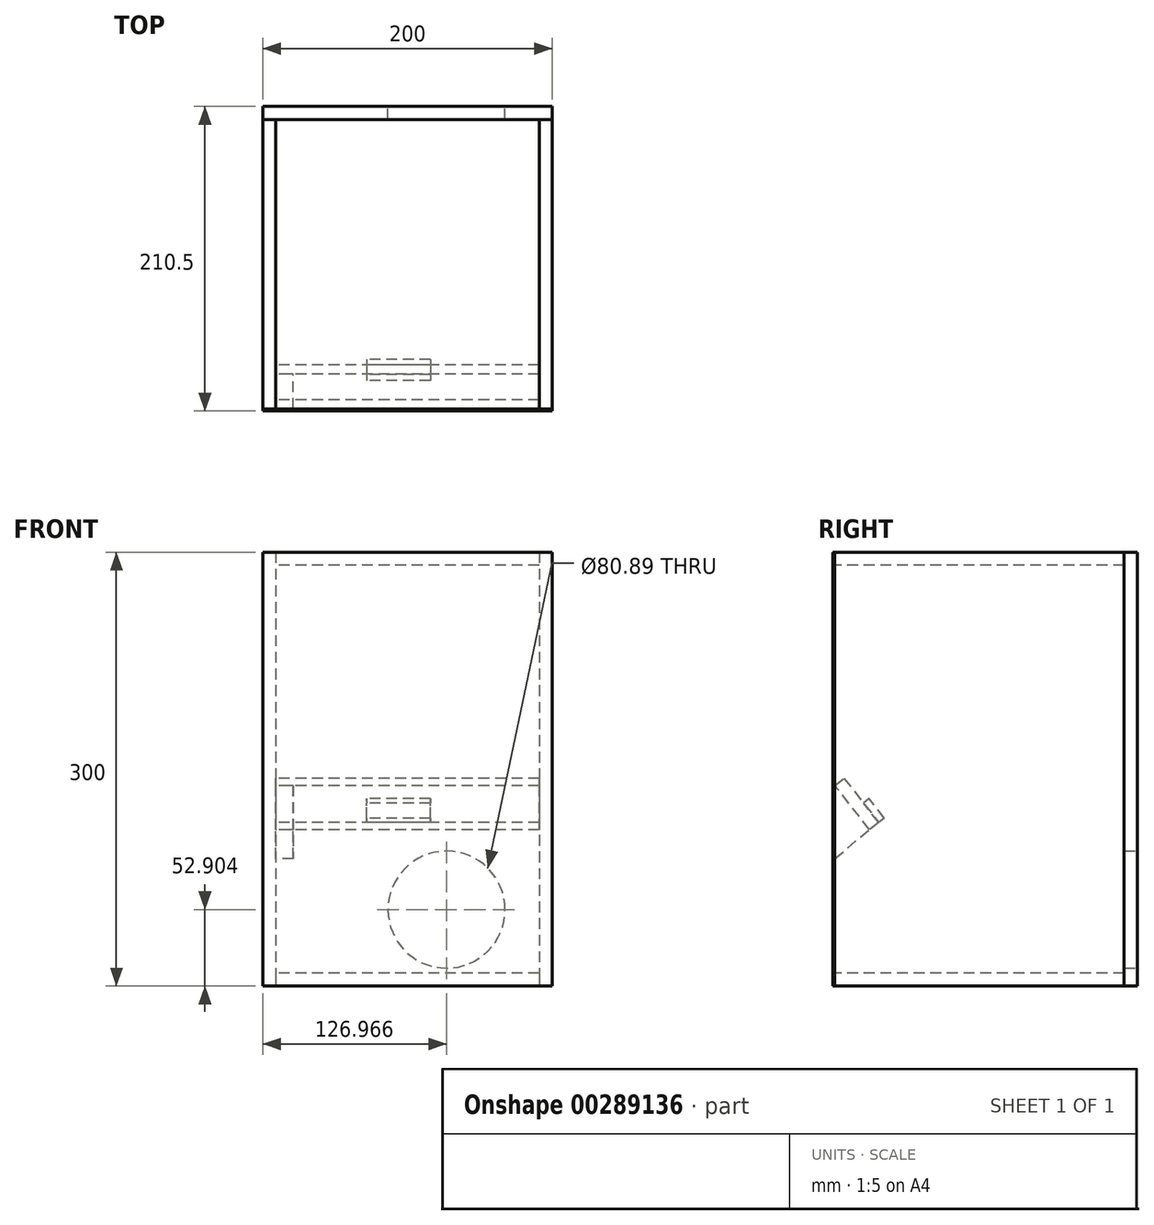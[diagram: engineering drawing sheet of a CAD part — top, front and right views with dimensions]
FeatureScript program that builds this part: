
annotation { "Feature Type Name" : "Feature", "Feature Type Description" : "" }
export const myFeature = defineFeature(function(context is Context, id is Id, definition is map)
    precondition{}
    {
        {
            var Q0;
            Q0=qCreatedBy(makeId("Front.planeOp"),FACE);
            var sketch = newSketch(context, id + "F0", { "sketchPlane" : qUnion([Q0])});
            skLineSegment(sketch, "E0.bottom", {"start": v(0, 0) * mm, "end": v(200, 0) * mm});
            skLineSegment(sketch, "E0.top", {"start": v(0, 300) * mm, "end": v(200, 300) * mm});
            skLineSegment(sketch, "E0.left", {"start": v(0, 0) * mm, "end": v(0, 300) * mm});
            skLineSegment(sketch, "E0.right", {"start": v(200, 0) * mm, "end": v(200, 300) * mm});
            skSolve(sketch);
        }
        {
            var Q0;
            Q0=qSketchRegion(id+"F0",true);
            extrude(context, id + "F1", {"entities" : qUnion([Q0]), "depth" : 1.5 * mm});
        }
        {
            var Q0;
            Q0=makeQuery(id+"F1.opExtrude","CAP_FACE",FACE,{"disambiguationData":[OSD([sQuery(id+"F0.wireOp",EDGE,"E0.bottom"),sQuery(id+"F0.wireOp",EDGE,"E0.top"),sQuery(id+"F0.wireOp",EDGE,"E0.left"),sQuery(id+"F0.wireOp",EDGE,"E0.right")])],"isStart":true});
            var sketch = newSketch(context, id + "F2", { "sketchPlane" : qUnion([Q0])});
            skLineSegment(sketch, "E1.bottom", {"start": v(0, 300) * mm, "end": v(-9, 300) * mm});
            skLineSegment(sketch, "E1.top", {"start": v(0, 0) * mm, "end": v(-9, 0) * mm});
            skLineSegment(sketch, "E1.left", {"start": v(0, 300) * mm, "end": v(0, 0) * mm});
            skLineSegment(sketch, "E1.right", {"start": v(-9, 300) * mm, "end": v(-9, 0) * mm});
            skSolve(sketch);
        }
        {
            var Q0;
            Q0=qSketchRegion(id+"F2",true);
            extrude(context, id + "F3", {"entities" : qUnion([Q0]), "depth" : 200 * mm});
        }
        {
            var Q0;
            Q0=makeQuery(id+"F3.opExtrude","SWEPT_FACE",FACE,{"disambiguationData":[OSD([sQuery(id+"F2.wireOp",EDGE,"E1.right")])]});
            var sketch = newSketch(context, id + "F4", { "sketchPlane" : qUnion([Q0])});
            skLineSegment(sketch, "E2", {"start": v(0, 138.7) * mm, "end": v(0, 88.15) * mm});
            skLineSegment(sketch, "E3", {"start": v(0, 88.15) * mm, "end": v(24, 108.1) * mm});
            skLineSegment(sketch, "E4", {"start": v(24, 108.1) * mm, "end": v(0, 138.7) * mm});
            skSolve(sketch);
        }
        {
            var Q0;
            Q0=qSketchRegion(id+"F4",true);
            extrude(context, id + "F5", {"entities" : qUnion([Q0]), "depth" : 12 * mm});
        }
        {
            var Q0;
            Q0=makeQuery(id+"F3.opExtrude","SWEPT_FACE",FACE,{"disambiguationData":[OSD([sQuery(id+"F2.wireOp",EDGE,"E1.right")])]});
            var sketch = newSketch(context, id + "F6", { "sketchPlane" : qUnion([Q0])});
            skLineSegment(sketch, "E5", {"start": v(24, 108.1) * mm, "end": v(0, 138.7) * mm});
            skLineSegment(sketch, "E6", {"start": v(0, 138.7) * mm, "end": v(6.36, 143.69) * mm});
            skLineSegment(sketch, "E7", {"start": v(6.36, 143.69) * mm, "end": v(30.36, 113.08) * mm});
            skLineSegment(sketch, "E8", {"start": v(30.36, 113.08) * mm, "end": v(24, 108.1) * mm});
            skSolve(sketch);
        }
        {
            var Q0;
            Q0=qSketchRegion(id+"F6",true);
            extrude(context, id + "F7", {"entities" : qUnion([Q0]), "depth" : 182 * mm});
        }
        {
            var Q0;
            Q0=makeQuery(id+"F7.opExtrude","SWEPT_FACE",FACE,{"disambiguationData":[OSD([sQuery(id+"F6.wireOp",EDGE,"E7")])]});
            var sketch = newSketch(context, id + "F8", { "sketchPlane" : qUnion([Q0])});
            skLineSegment(sketch, "E9.bottom", {"start": v(-115.8, 70.24) * mm, "end": v(-71.6, 70.24) * mm});
            skLineSegment(sketch, "E9.top", {"start": v(-115.8, 87.47) * mm, "end": v(-71.6, 87.47) * mm});
            skLineSegment(sketch, "E9.left", {"start": v(-115.8, 70.24) * mm, "end": v(-115.8, 87.47) * mm});
            skLineSegment(sketch, "E9.right", {"start": v(-71.6, 70.24) * mm, "end": v(-71.6, 87.47) * mm});
            skSolve(sketch);
        }
        {
            var Q0;
            Q0=qSketchRegion(id+"F8",true);
            extrude(context, id + "F9", {"entities" : qUnion([Q0]), "depth" : 5 * mm});
        }
        {
            var Q0;
            Q0=makeQuery(id+"F3.opExtrude","SWEPT_FACE",FACE,{"disambiguationData":[OSD([sQuery(id+"F2.wireOp",EDGE,"E1.right")])]});
            var sketch = newSketch(context, id + "F10", { "sketchPlane" : qUnion([Q0])});
            skLineSegment(sketch, "E10.bottom", {"start": v(200, 300) * mm, "end": v(0, 300) * mm});
            skLineSegment(sketch, "E10.top", {"start": v(200, 291) * mm, "end": v(0, 291) * mm});
            skLineSegment(sketch, "E10.left", {"start": v(200, 300) * mm, "end": v(200, 291) * mm});
            skLineSegment(sketch, "E10.right", {"start": v(0, 300) * mm, "end": v(0, 291) * mm});
            skSolve(sketch);
        }
        {
            var Q0;
            Q0=qSketchRegion(id+"F10",true);
            extrude(context, id + "F11", {"entities" : qUnion([Q0]), "depth" : 182 * mm});
        }
        {
            var Q0;
            Q0=makeQuery(id+"F3.opExtrude","SWEPT_FACE",FACE,{"disambiguationData":[OSD([sQuery(id+"F2.wireOp",EDGE,"E1.right")])]});
            var sketch = newSketch(context, id + "F12", { "sketchPlane" : qUnion([Q0])});
            skLineSegment(sketch, "E11.bottom", {"start": v(200, 0) * mm, "end": v(0, 0) * mm});
            skLineSegment(sketch, "E11.top", {"start": v(200, 9) * mm, "end": v(0, 9) * mm});
            skLineSegment(sketch, "E11.left", {"start": v(200, 0) * mm, "end": v(200, 9) * mm});
            skLineSegment(sketch, "E11.right", {"start": v(0, 0) * mm, "end": v(0, 9) * mm});
            skSolve(sketch);
        }
        {
            var Q0;
            Q0=qSketchRegion(id+"F12",true);
            extrude(context, id + "F13", {"entities" : qUnion([Q0]), "depth" : 182 * mm});
        }
        {
            var Q0;
            Q0=makeQuery(id+"F11.opExtrude","CAP_FACE",FACE,{"disambiguationData":[OSD([sQuery(id+"F10.wireOp",EDGE,"E10.bottom"),sQuery(id+"F10.wireOp",EDGE,"E10.top"),sQuery(id+"F10.wireOp",EDGE,"E10.left"),sQuery(id+"F10.wireOp",EDGE,"E10.right")])],"isStart":false});
            var sketch = newSketch(context, id + "F14", { "sketchPlane" : qUnion([Q0])});
            skLineSegment(sketch, "E12.bottom", {"start": v(200, 300) * mm, "end": v(0, 300) * mm});
            skLineSegment(sketch, "E12.top", {"start": v(200, 0) * mm, "end": v(0, 0) * mm});
            skLineSegment(sketch, "E12.left", {"start": v(200, 300) * mm, "end": v(200, 0) * mm});
            skLineSegment(sketch, "E12.right", {"start": v(0, 300) * mm, "end": v(0, 0) * mm});
            skSolve(sketch);
        }
        {
            var Q0;
            Q0=qSketchRegion(id+"F14",true);
            extrude(context, id + "F15", {"entities" : qUnion([Q0]), "depth" : 9 * mm});
        }
        {
            var Q0;
            Q0=makeQuery(id+"F15.opExtrude","SWEPT_FACE",FACE,{"disambiguationData":[OSD([sQuery(id+"F14.wireOp",EDGE,"E12.left")])]});
            var sketch = newSketch(context, id + "F16", { "sketchPlane" : qUnion([Q0])});
            skLineSegment(sketch, "E13.bottom", {"start": v(-200, 300) * mm, "end": v(0, 300) * mm});
            skLineSegment(sketch, "E13.top", {"start": v(-200, 0) * mm, "end": v(0, 0) * mm});
            skLineSegment(sketch, "E13.left", {"start": v(-200, 300) * mm, "end": v(-200, 0) * mm});
            skLineSegment(sketch, "E13.right", {"start": v(0, 300) * mm, "end": v(0, 0) * mm});
            skSolve(sketch);
        }
        {
            var Q0;
            Q0=qSketchRegion(id+"F16",true);
            extrude(context, id + "F17", {"entities" : qUnion([Q0]), "depth" : 9 * mm});
        }
        {
            var Q0;
            Q0=makeQuery(id+"F17.opExtrude","CAP_FACE",FACE,{"disambiguationData":[OSD([sQuery(id+"F16.wireOp",EDGE,"E13.bottom"),sQuery(id+"F16.wireOp",EDGE,"E13.top"),sQuery(id+"F16.wireOp",EDGE,"E13.left"),sQuery(id+"F16.wireOp",EDGE,"E13.right")])],"isStart":false});
            var sketch = newSketch(context, id + "F18", { "sketchPlane" : qUnion([Q0])});
            skCircle(sketch, "E14", {"center": v(-126.97, 52.9) * mm, "radius": 40.44 * mm});
            skSolve(sketch);
        }
        {
            var Q0;
            Q0=qSketchRegion(id+"F18",true);
            extrude(context, id + "F19", {"entities" : qUnion([Q0]), "operationType" : NewBodyOperationType.REMOVE, "oppositeDirection" : true, "depth" : 9 * mm});
        }
        {
            var Q0;
            Q0=makeQuery(id+"F13.opExtrude","SWEPT_FACE",FACE,{"disambiguationData":[OSD([sQuery(id+"F12.wireOp",EDGE,"E11.bottom")])]});
            var sketch = newSketch(context, id + "F20", { "sketchPlane" : qUnion([Q0])});
            skLineSegment(sketch, "E15.bottom", {"start": v(200, 0) * mm, "end": v(177, 0) * mm});
            skLineSegment(sketch, "E15.top", {"start": v(200, -23) * mm, "end": v(177, -23) * mm});
            skLineSegment(sketch, "E15.left", {"start": v(200, 0) * mm, "end": v(200, -23) * mm});
            skLineSegment(sketch, "E15.right", {"start": v(177, 0) * mm, "end": v(177, -23) * mm});
            skSolve(sketch);
        }
        {
            var Q0;
            Q0=qSketchRegion(id+"F20",true);
            extrude(context, id + "F21", {"entities" : qUnion([Q0]), "depth" : 10 * mm});
        }
        {
            var Q0;
            Q0=makeQuery(id+"F13.opExtrude","SWEPT_FACE",FACE,{"disambiguationData":[OSD([sQuery(id+"F12.wireOp",EDGE,"E11.bottom")])]});
            var sketch = newSketch(context, id + "F22", { "sketchPlane" : qUnion([Q0])});
            skLineSegment(sketch, "E16.bottom", {"start": v(0, -209.08) * mm, "end": v(23, -209.08) * mm});
            skLineSegment(sketch, "E16.top", {"start": v(0, -186.08) * mm, "end": v(23, -186.08) * mm});
            skLineSegment(sketch, "E16.left", {"start": v(0, -209.08) * mm, "end": v(0, -186.08) * mm});
            skLineSegment(sketch, "E16.right", {"start": v(23, -209.08) * mm, "end": v(23, -186.08) * mm});
            skSolve(sketch);
        }
        {
            var Q0;
            Q0=qSketchRegion(id+"F22",true);
            extrude(context, id + "F23", {"entities" : qUnion([Q0]), "depth" : 10 * mm});
        }
        {
            var Q0;
            Q0=makeQuery(id+"F13.opExtrude","SWEPT_FACE",FACE,{"disambiguationData":[OSD([sQuery(id+"F12.wireOp",EDGE,"E11.bottom")])]});
            var sketch = newSketch(context, id + "F24", { "sketchPlane" : qUnion([Q0])});
            skLineSegment(sketch, "E17.bottom", {"start": v(200, -209) * mm, "end": v(177, -209) * mm});
            skLineSegment(sketch, "E17.top", {"start": v(200, -186) * mm, "end": v(177, -186) * mm});
            skLineSegment(sketch, "E17.left", {"start": v(200, -209) * mm, "end": v(200, -186) * mm});
            skLineSegment(sketch, "E17.right", {"start": v(177, -209) * mm, "end": v(177, -186) * mm});
            skSolve(sketch);
        }
        {
            var Q0;
            Q0=qSketchRegion(id+"F24",true);
            extrude(context, id + "F25", {"entities" : qUnion([Q0]), "depth" : 10 * mm});
        }
        {
            var Q0;
            Q0=makeQuery(id+"F25.opExtrude","SWEPT_BODY",BODY,{"disambiguationData":[OSD([sQuery(id+"F24.wireOp",EDGE,"E17.bottom"),sQuery(id+"F24.wireOp",EDGE,"E17.top"),sQuery(id+"F24.wireOp",EDGE,"E17.left"),sQuery(id+"F24.wireOp",EDGE,"E17.right")])]});
            var Q1;
            Q1=makeQuery(id+"F23.opExtrude","SWEPT_BODY",BODY,{"disambiguationData":[OSD([sQuery(id+"F22.wireOp",EDGE,"E16.bottom"),sQuery(id+"F22.wireOp",EDGE,"E16.top"),sQuery(id+"F22.wireOp",EDGE,"E16.left"),sQuery(id+"F22.wireOp",EDGE,"E16.right")])]});
            var Q2;
            Q2=makeQuery(id+"F21.opExtrude","SWEPT_BODY",BODY,{"disambiguationData":[OSD([sQuery(id+"F20.wireOp",EDGE,"E15.bottom"),sQuery(id+"F20.wireOp",EDGE,"E15.top"),sQuery(id+"F20.wireOp",EDGE,"E15.left"),sQuery(id+"F20.wireOp",EDGE,"E15.right")])]});
            var Q3;
            Q3=makeQuery(id+"Fs5yDIBLOdXcwiO_9.opExtrude","SWEPT_BODY",BODY,{"disambiguationData":[OSD([sQuery(id+"FYxa9HawI8RwomP_9.wireOp",EDGE,"8wPZq0gx-ZW2F-fVTf-aa48-C1ibRZGlh671.bottom"),sQuery(id+"FYxa9HawI8RwomP_9.wireOp",EDGE,"8wPZq0gx-ZW2F-fVTf-aa48-C1ibRZGlh671.top"),sQuery(id+"FYxa9HawI8RwomP_9.wireOp",EDGE,"8wPZq0gx-ZW2F-fVTf-aa48-C1ibRZGlh671.left"),sQuery(id+"FYxa9HawI8RwomP_9.wireOp",EDGE,"8wPZq0gx-ZW2F-fVTf-aa48-C1ibRZGlh671.right")])]});
            deleteBodies(context, id + "F26", {"entities" : qUnion([Q0, Q1, Q2, Q3])});
        }
    });
